# Revit family: O14761001 Lavamanos Spazio
name_source: partatom
category: Generic Models
units: mm (PartAtom-declared; Revit-internal decimal feet)

## family parameters
Can host rebar = No
Cut with Voids When Loaded = No
Host = Face
OmniClass Number = 23.31.13.11
OmniClass Title = Single Sinks
Part Type = Normal
Room Calculation Point = No
Round Connector Dimension = Use Diameter
Shared = No

## types (2) — shared parameters
Alto = 864 mm
Ancho = 375 mm  [stored 1.23031 ft]
Creado por = IDD
Default Elevation = 1219 mm
Description = Lavamanos tipo vessel en porcelana sanitaria. 
Cumple con los requerimientos ADA.
Dimensiones del producto empacado = 16 1/8” x 16 1/8” x 6 1/4” (41 cm x 41 cm x 16 cm)
Fecha de creación = 17/07/2020
Garantía = Limitada de por vida CORONA
Manufacturer = Corona
Peso del producto empacado = 5.3 kgs
Pozo = 3 3/4” x 4 3/4” (35.5 cm x 12 cm)
Profundidad = 375 mm  [stored 1.23031 ft]
URL = https://corona.co

## per-type parameters (varying)
| type | Material |
| Spazio 100 Blanco | Corona_Porcelana_Sanitaria |
| Spazio 103 Bone | Corona_Porcelana_Sanitaria_Bone |

note: [stored X ft] marks values corroborated as IEEE doubles in the binary element streams (Revit-internal decimal feet)

## geometry (parser evidence)
native form markers: Sweep x6
no freeform markers — native parametric forms only
